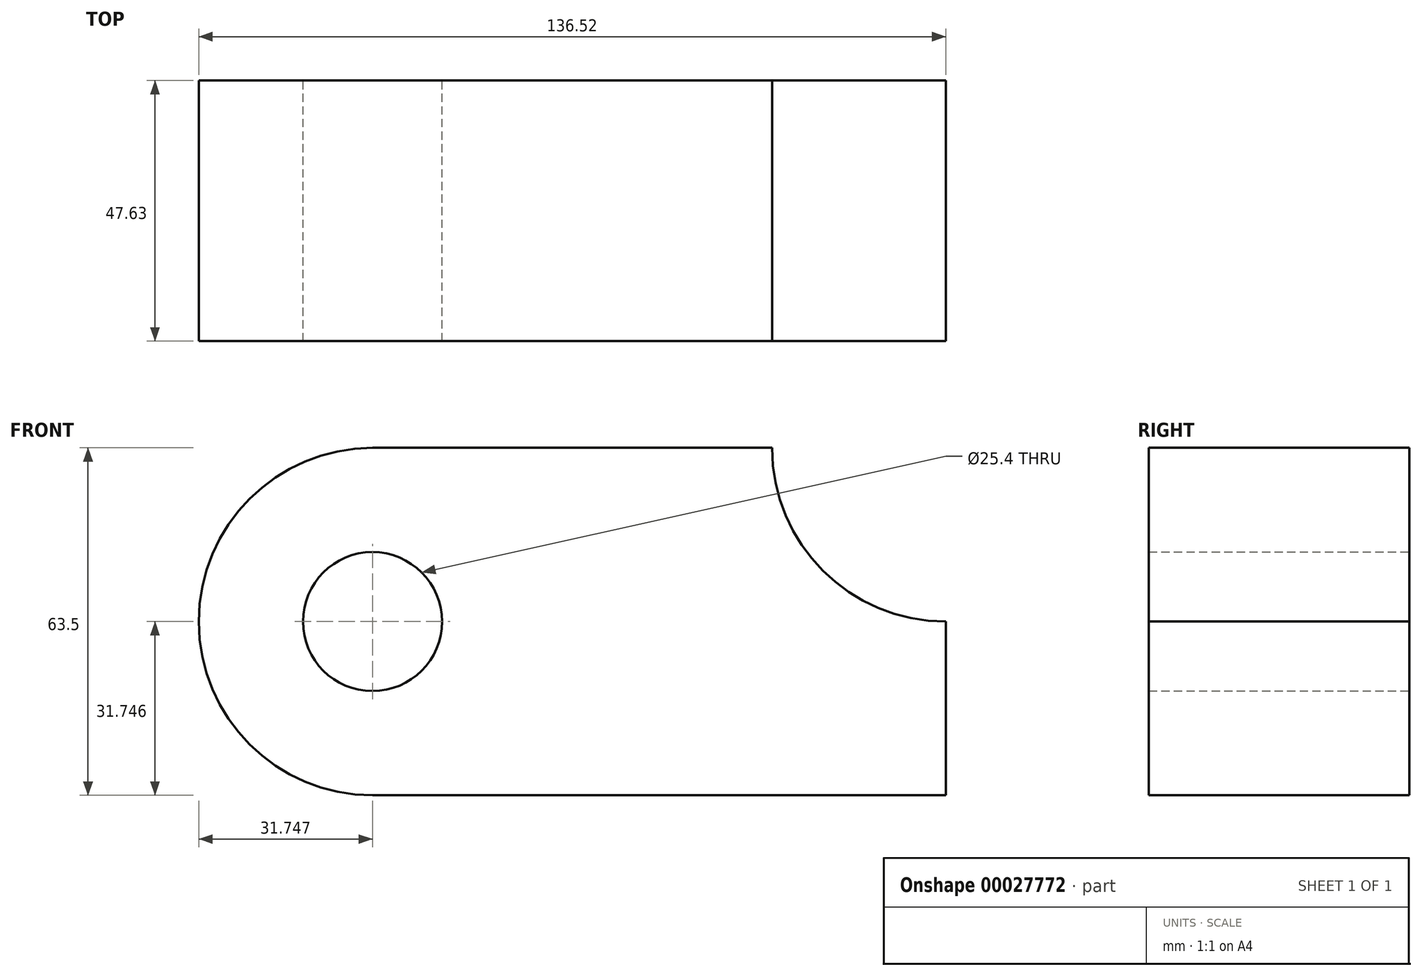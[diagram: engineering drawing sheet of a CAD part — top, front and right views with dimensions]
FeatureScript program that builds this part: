
annotation { "Feature Type Name" : "Feature", "Feature Type Description" : "" }
export const myFeature = defineFeature(function(context is Context, id is Id, definition is map)
    precondition{}
    {
        {
            var Q0;
            Q0=qCreatedBy(makeId("Front.planeOp"),FACE);
            var sketch = newSketch(context, id + "F0", { "sketchPlane" : qUnion([Q0])});
            skLineSegment(sketch, "E0.bottom", {"start": v(-70.87, 32.65) * mm, "end": v(33.9, 32.65) * mm});
            skLineSegment(sketch, "E0.top", {"start": v(-70.87, -30.85) * mm, "end": v(33.9, -30.85) * mm});
            skLineSegment(sketch, "E0.left", {"start": v(-70.87, 32.65) * mm, "end": v(-70.87, -30.85) * mm});
            skLineSegment(sketch, "E0.right", {"start": v(33.9, 32.65) * mm, "end": v(33.9, -30.85) * mm});
            skCircle(sketch, "E1", {"center": v(-70.87, 0.9) * mm, "radius": 31.75 * mm});
            skCircle(sketch, "E2", {"center": v(33.9, 32.65) * mm, "radius": 31.75 * mm});
            skCircle(sketch, "E3", {"center": v(-70.87, 0.9) * mm, "radius": 12.7 * mm});
            skSolve(sketch);
        }
        {
            var Q0;
            {var subQ1=sQuery(id+"F0.wireOp",EDGE,"E0.left");Q0=makeQuery(id+"F0.imprint","IMPRINT",FACE,{"disambiguationData":[TD([[makeQuery(id+"F0.imprint","IMPRINT",EDGE,{"derivedFrom":subQ1}),-1.0]])]});}
            var Q1;
            {var subQ1=sQuery(id+"F0.wireOp",EDGE,"E0.left");Q1=makeQuery(id+"F0.imprint","IMPRINT",FACE,{"disambiguationData":[TD([[makeQuery(id+"F0.imprint","IMPRINT",EDGE,{"derivedFrom":subQ1}),1.0]])]});}
            var Q2;
            {var subQ5=sQuery(id+"F0.wireOp",EDGE,"E0.top");Q2=makeQuery(id+"F0.imprint","IMPRINT",FACE,{"disambiguationData":[TD([[makeQuery(id+"F0.imprint","IMPRINT",EDGE,{"derivedFrom":subQ5}),1.0]])]});}
            extrude(context, id + "F1", {"entities" : qUnion([Q0, Q1, Q2]), "depth" : 47.62 * mm});
        }
    });
